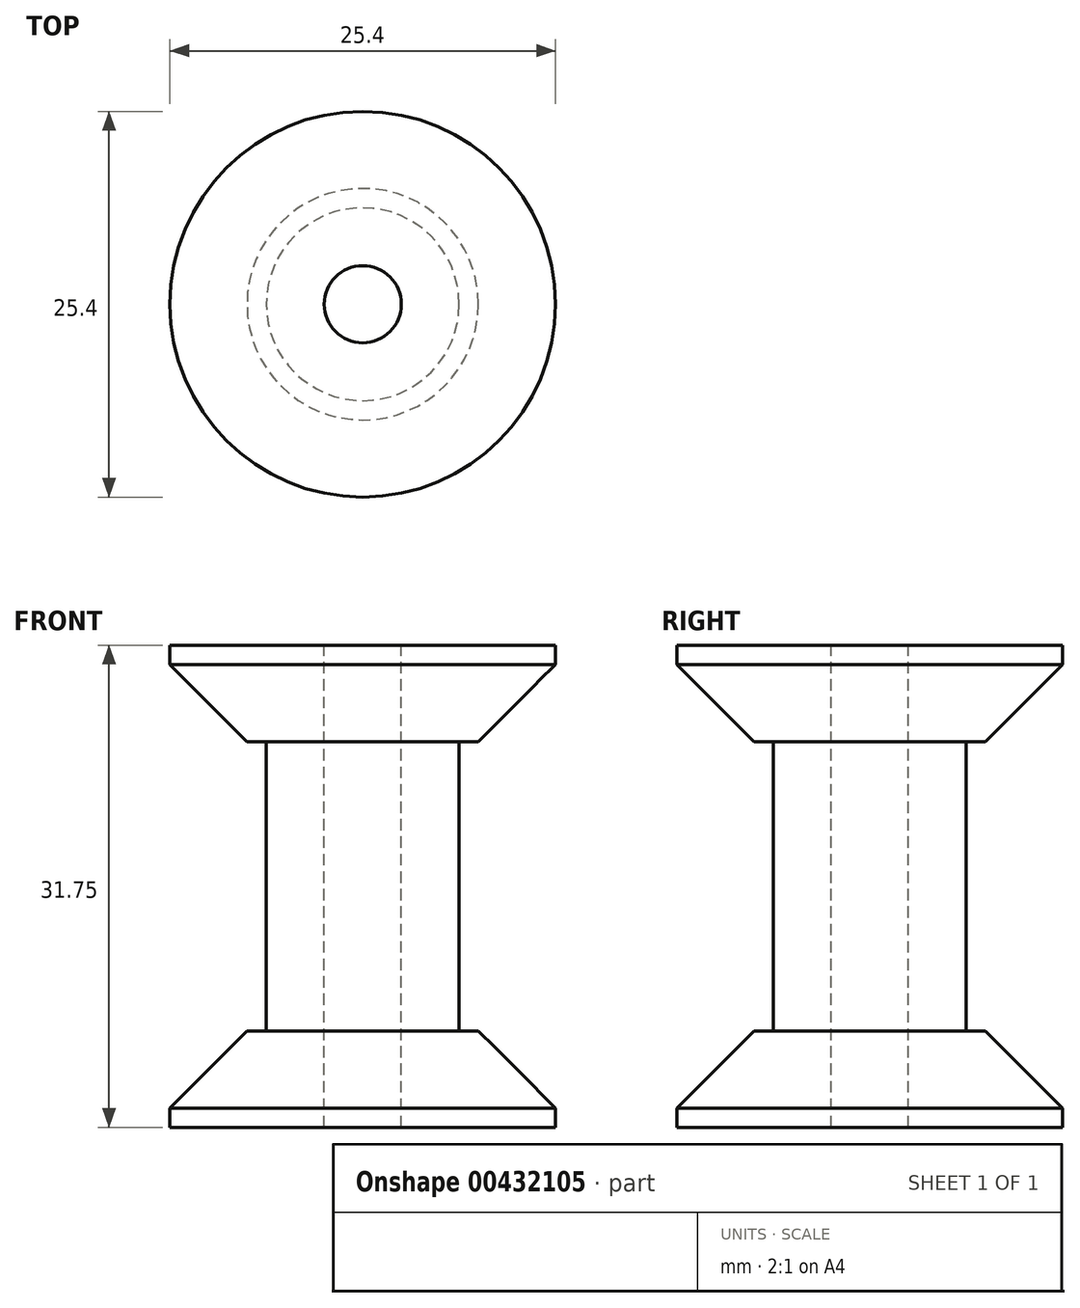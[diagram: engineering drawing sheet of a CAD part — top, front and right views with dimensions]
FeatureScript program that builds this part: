
annotation { "Feature Type Name" : "Feature", "Feature Type Description" : "" }
export const myFeature = defineFeature(function(context is Context, id is Id, definition is map)
    precondition{}
    {
        {
            var Q0;
            Q0=qCreatedBy(makeId("Top.planeOp"),FACE);
            var sketch = newSketch(context, id + "F0", { "sketchPlane" : qUnion([Q0])});
            skCircle(sketch, "E0", {"center": v(0, 0) * mm, "radius": 12.7 * mm});
            skSolve(sketch);
        }
        {
            var Q0;
            Q0 = qSketchRegion(id + "F0", true);
            extrude(context, id + "F1", {"entities" : qUnion([Q0]), "depth" : 6.35 * mm});
        }
        {
            var Q0;
            Q0=qCreatedBy(makeId("Top.planeOp"),FACE);
            var sketch = newSketch(context, id + "F2", { "sketchPlane" : qUnion([Q0])});
            skCircle(sketch, "E1", {"center": v(0, 0) * mm, "radius": 6.35 * mm});
            skSolve(sketch);
        }
        {
            var Q0;
            Q0 = qSketchRegion(id + "F2", true);
            extrude(context, id + "F3", {"entities" : qUnion([Q0]), "operationType" : NewBodyOperationType.ADD, "depth" : 25.4 * mm});
        }
        {
            var Q0;
            Q0=makeQuery(id+"F3.opExtrude","CAP_FACE",FACE,{"disambiguationData":[OSD([sQuery(id+"F2.wireOp",EDGE,"E1")])],"isStart":false});
            var sketch = newSketch(context, id + "F4", { "sketchPlane" : qUnion([Q0])});
            skCircle(sketch, "E2", {"center": v(0, 0) * mm, "radius": 12.7 * mm});
            skSolve(sketch);
        }
        {
            var Q0;
            Q0=makeQuery(id+"F4.imprint","IMPRINT",FACE,{"disambiguationData":[TD([[makeQuery(id+"F4.imprint","IMPRINT",EDGE,{"derivedFrom":makeQuery(id+"F3.opExtrude","CAP_EDGE",EDGE,{"disambiguationData":[OSD([sQuery(id+"F2.wireOp",EDGE,"E1")])],"isStart":false})}),1.0]])]});
            var sketch = newSketch(context, id + "F5", { "sketchPlane" : qUnion([Q0])});
            skCircle(sketch, "E3", {"center": v(0, 0) * mm, "radius": 12.7 * mm});
            skSolve(sketch);
        }
        {
            var Q0;
            Q0 = qSketchRegion(id + "F5", true);
            extrude(context, id + "F6", {"entities" : qUnion([Q0]), "operationType" : NewBodyOperationType.ADD, "depth" : 6.35 * mm});
        }
        {
            var Q0;
            Q0=makeQuery(id+"F6.opExtrude","CAP_FACE",FACE,{"disambiguationData":[OSD([sQuery(id+"F5.wireOp",EDGE,"E3")])],"isStart":false});
            var sketch = newSketch(context, id + "F7", { "sketchPlane" : qUnion([Q0])});
            skCircle(sketch, "E4", {"center": v(0, 0) * mm, "radius": 2.54 * mm});
            skSolve(sketch);
        }
        {
            var Q0;
            Q0 = qSketchRegion(id + "F7", true);
            extrude(context, id + "F8", {"entities" : qUnion([Q0]), "operationType" : NewBodyOperationType.REMOVE, "oppositeDirection" : true, "depth" : 31.75 * mm});
        }
        {
            var Q0;
            Q0=makeQuery(id+"F6.opExtrude","CAP_EDGE",EDGE,{"disambiguationData":[OSD([sQuery(id+"F5.wireOp",EDGE,"E3")])],"isStart":true});
            var Q1;
            Q1=makeQuery(id+"F1.opExtrude","CAP_EDGE",EDGE,{"disambiguationData":[OSD([sQuery(id+"F0.wireOp",EDGE,"E0")])],"isStart":false});
            chamfer(context, id + "F9", {"entities" : qUnion([Q0, Q1]), "width" : 5.08 * mm, "tangentPropagation" : true});
        }
    });
